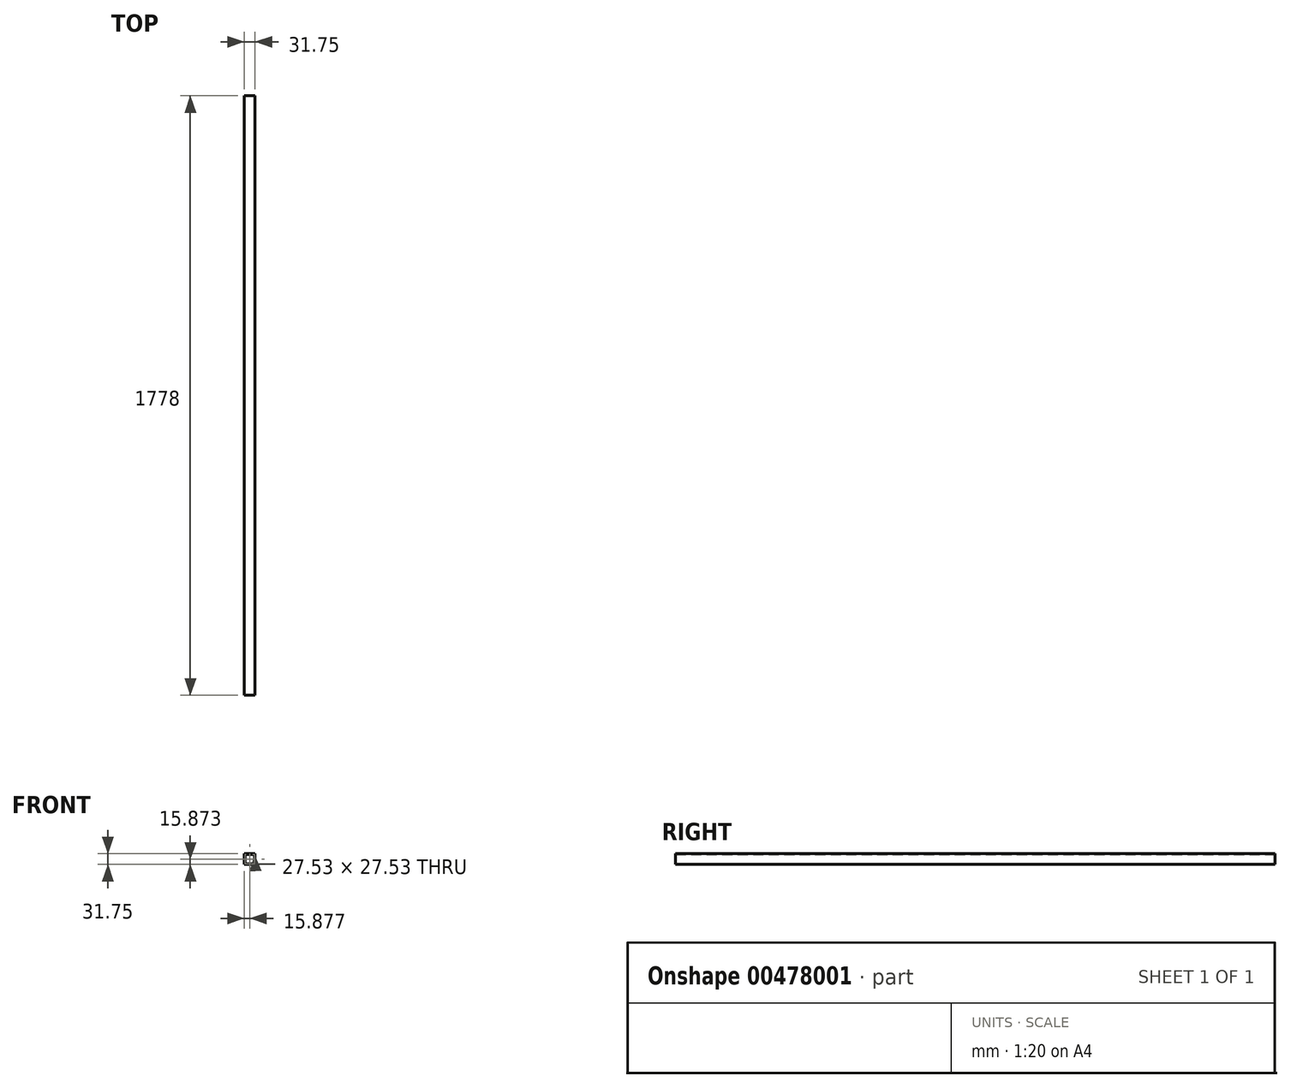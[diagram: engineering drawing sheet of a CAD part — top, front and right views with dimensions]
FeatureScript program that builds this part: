
annotation { "Feature Type Name" : "Feature", "Feature Type Description" : "" }
export const myFeature = defineFeature(function(context is Context, id is Id, definition is map)
    precondition{}
    {
        {
            var Q0;
            Q0=qCreatedBy(makeId("Front.planeOp"),FACE);
            var sketch = newSketch(context, id + "F0", { "sketchPlane" : qUnion([Q0])});
            skLineSegment(sketch, "E0.bottom", {"start": v(-45.93, 18.33) * mm, "end": v(-14.18, 18.33) * mm});
            skLineSegment(sketch, "E0.top", {"start": v(-45.93, -13.42) * mm, "end": v(-14.18, -13.42) * mm});
            skLineSegment(sketch, "E0.left", {"start": v(-45.93, 18.33) * mm, "end": v(-45.93, -13.42) * mm});
            skLineSegment(sketch, "E0.right", {"start": v(-14.18, 18.33) * mm, "end": v(-14.18, -13.42) * mm});
            skLineSegment(sketch, "E1.0", {"start": v(-16.29, 16.22) * mm, "end": v(-16.29, -11.31) * mm});
            skLineSegment(sketch, "E1.1", {"start": v(-43.82, 16.22) * mm, "end": v(-16.29, 16.22) * mm});
            skLineSegment(sketch, "E1.2", {"start": v(-43.82, 16.22) * mm, "end": v(-43.82, -11.31) * mm});
            skLineSegment(sketch, "E1.3", {"start": v(-43.82, -11.31) * mm, "end": v(-16.29, -11.31) * mm});
            skSolve(sketch);
        }
        {
            var Q0;
            Q0=qSketchRegion(id+"F0",true);
            extrude(context, id + "F1", {"entities" : qUnion([Q0]), "depth" : 1778 * mm});
        }
    });
